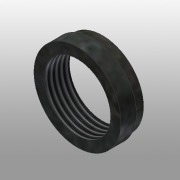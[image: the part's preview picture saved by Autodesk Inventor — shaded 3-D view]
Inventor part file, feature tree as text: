
AUTODESK INVENTOR PART (.ipt)
format: ipt  version: 2016 (Build 200138000, 138)  size: 113,152 bytes
history: native  units: mm
features: sketch x3, extrude x2, hole x1
ambient origin geometry x8: Origin, YZ Plane, XZ Plane, XY Plane, X Axis, Y Axis, Z Axis, Center Point
bodies: Solid1 (feature_tree)
feature tree (6):
  extrude  "Extrusion1"  Depth=3.0mm TaperAngle=0.0deg
  extrude  "Extrusion2"  Depth=1.9mm TaperAngle=0.0deg
  hole  "Hole1"  [1 undecoded]
  sketch  "Sketch1"  dims[d0=17.0mm d1=3.0mm d2=0.0mm]
  sketch  "Sketch2"  dims[d3=16.0mm d4=1.9mm d5=0.0mm]
  sketch  "Sketch3"  dims[d6=12.917mm d7=28.0mm d8=4.0mm d9=2.0mm d10=90.0deg d11=33.1mm d12=20.594885mm]
note: 1 required parameter value undecoded (feature->parameter linkage not recoverable at this tier; creation-order binding heuristic only, values carry confidence <= 0.55)
